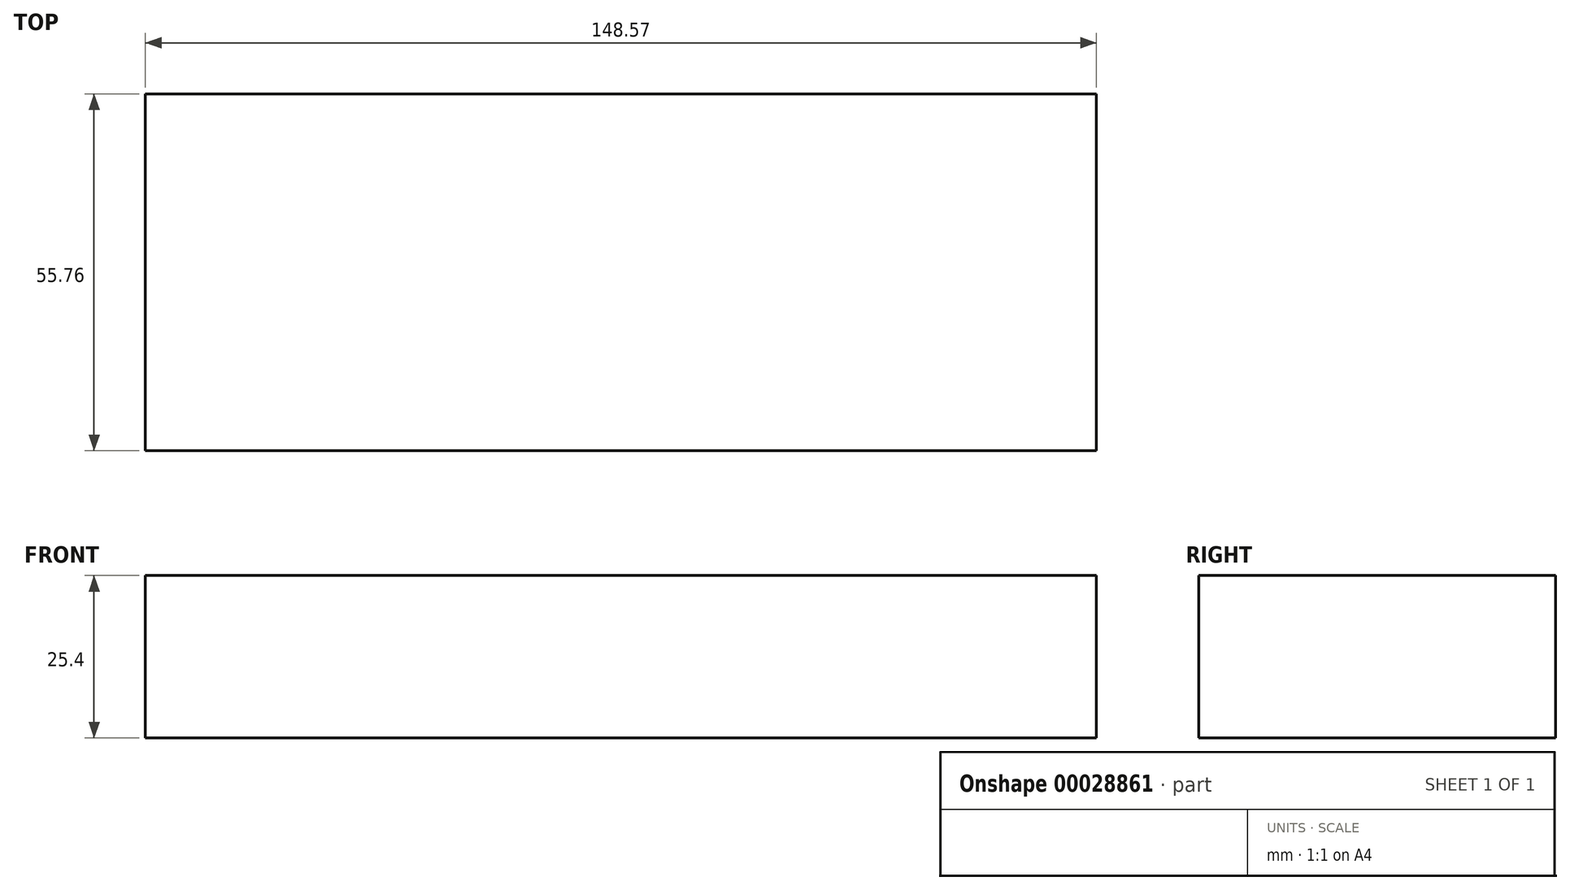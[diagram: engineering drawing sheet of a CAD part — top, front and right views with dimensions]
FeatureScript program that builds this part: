
annotation { "Feature Type Name" : "Feature", "Feature Type Description" : "" }
export const myFeature = defineFeature(function(context is Context, id is Id, definition is map)
    precondition{}
    {
        {
            var Q0;
            Q0=qCreatedBy(makeId("Top.planeOp"),FACE);
            var sketch = newSketch(context, id + "F0", { "sketchPlane" : qUnion([Q0])});
            skLineSegment(sketch, "E0", {"start": v(-86.55, 28.9) * mm, "end": v(-86.55, -26.85) * mm});
            skLineSegment(sketch, "E1", {"start": v(-86.55, -26.85) * mm, "end": v(62.02, -26.85) * mm});
            skLineSegment(sketch, "E2", {"start": v(62.02, -26.85) * mm, "end": v(62.02, 28.9) * mm});
            skLineSegment(sketch, "E3", {"start": v(62.02, 28.9) * mm, "end": v(-86.6, 28.9) * mm});
            skSolve(sketch);
        }
        {
            var Q0;
            {var subQ2=sQuery(id+"F0.wireOp",EDGE,"E0");Q0=makeQuery(id+"F0.imprint","IMPRINT",FACE,{"disambiguationData":[TD([[makeQuery(id+"F0.imprint","IMPRINT",EDGE,{"derivedFrom":subQ2}),1.0]])]});}
            extrude(context, id + "F1", {"entities" : qUnion([Q0]), "depth" : 25.4 * mm});
        }
    });
